# Revit family: Window_Shade-Draper-Bottom-Up_FlexShade
name_source: partatom
category: Specialty Equipment
units: mm (PartAtom-declared; Revit-internal decimal feet)

## family parameters
Always vertical = Yes
Classification Number = 23.30.20.11
Cut with Voids When Loaded = No
Enable Cutting in Views = No
Maintain Annotation Orientation = No
Part Type = Normal
Room Calculation Point = No
Round Connector Dimension = Use Diameter
Shared = No
Work Plane-Based = No

## types (3) — shared parameters
Casing = Metal - Draper - Clear Anodized
Continuous Chain = Metal - Draper - Black
Custom Sizes = Custom Sizes are availabe in many shade fabrics dpending on the roller diameter.
Default Elevation = 0' - 0"
Depth = 0' - 0"
Description = Interior Window Shade
Manufacturer = Draper
Model = FlexShade
Product Name = Bottom-Up FlexShade
Shade Fabric = Fabric - Draper - Screen
URL = http://www.draperinc.com

## per-type parameters (varying)
| type | Brackets | Motorized | Product Page URL | XD Clutch |
| XD Clutch | Yes | No | http://www.draperinc.com | Yes |
| Motorized | Yes | Yes | www.draperinc.com/go/BottomUp.htm | No |
| Motorized Dual Roller | No | No | http://www.draperinc.com | No |

type visibility flags (boolean, named after types; folded from table):
- XD Clutch: Yes: (none)
- Motorized: Yes: (none)
- Motorized Dual Roller: Yes: Motorized Dual Roller

## geometry (parser evidence)
native form markers: Blend x9, Sweep x5
no freeform markers — native parametric forms only
